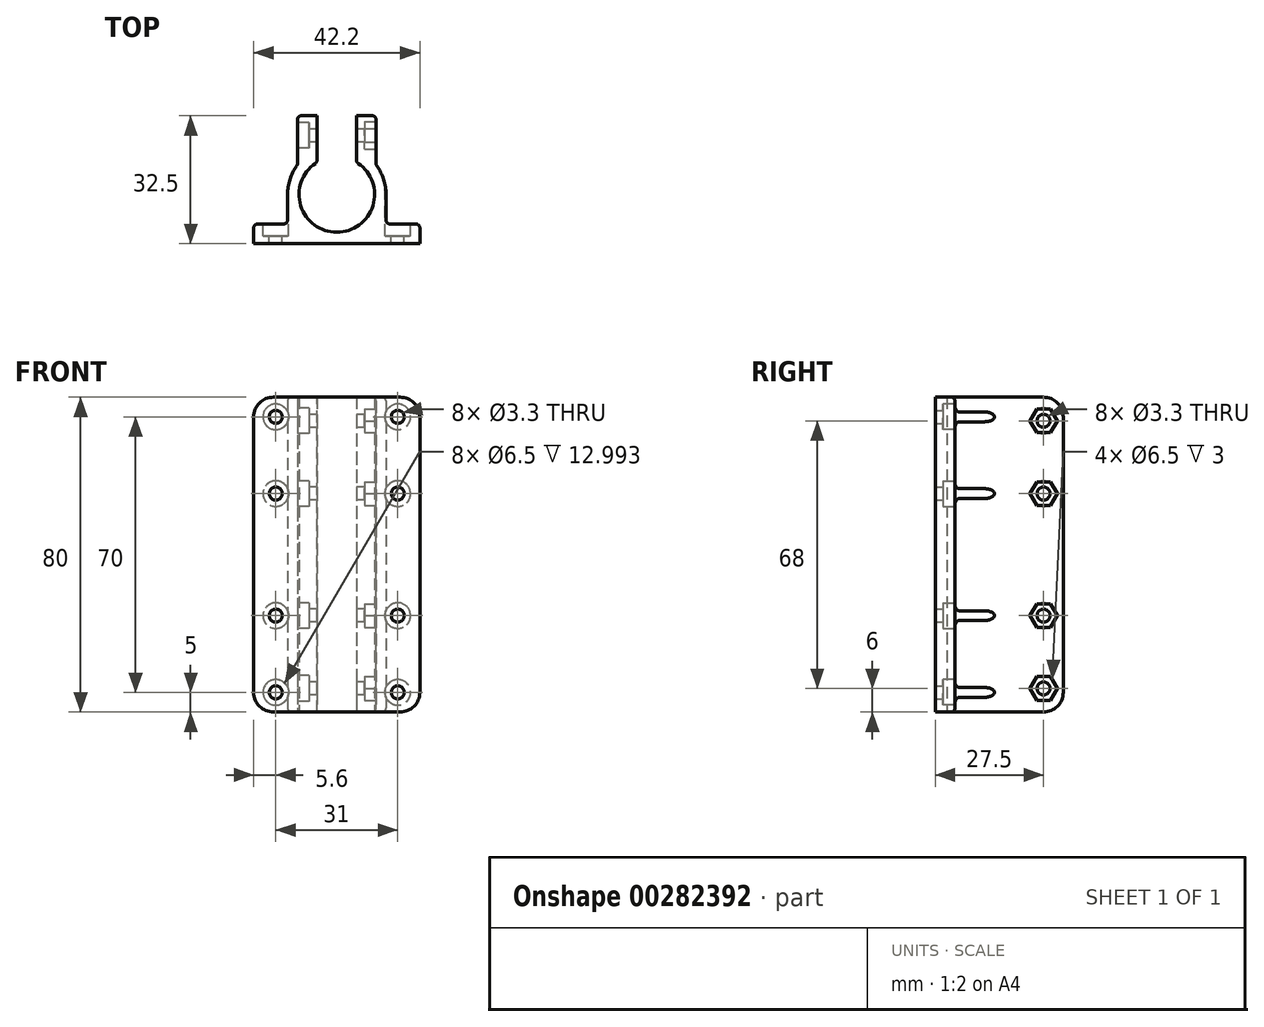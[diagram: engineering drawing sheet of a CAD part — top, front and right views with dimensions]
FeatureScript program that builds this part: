
annotation { "Feature Type Name" : "Feature", "Feature Type Description" : "" }
export const myFeature = defineFeature(function(context is Context, id is Id, definition is map)
    precondition{}
    {
        {
            var Q0;
            Q0=qCreatedBy(makeId("Top.planeOp"),FACE);
            var sketch = newSketch(context, id + "F0", { "sketchPlane" : qUnion([Q0])});
            skArc(sketch, "E0", {"start": v(-5, 8.2) * mm, "mid": v(0, -9.6) * mm, "end": v(5, 8.2) * mm});
            skArc(sketch, "E1", {"start": v(12.5, 0) * mm, "mid": v(11.86, 3.95) * mm, "end": v(10, 7.5) * mm});
            skLineSegment(sketch, "E2", {"start": v(0, 0) * mm, "end": v(0, -12.5) * mm, "construction": true});
            skLineSegment(sketch, "E3", {"start": v(0, -12.5) * mm, "end": v(21.1, -12.5) * mm});
            skLineSegment(sketch, "E4", {"start": v(21.1, -12.5) * mm, "end": v(21.1, -7.5) * mm});
            skLineSegment(sketch, "E5", {"start": v(0, -12.5) * mm, "end": v(-21.1, -12.5) * mm});
            skLineSegment(sketch, "E6", {"start": v(-21.1, -12.5) * mm, "end": v(-21.1, -7.5) * mm});
            skLineSegment(sketch, "E7", {"start": v(-12.5, -7.5) * mm, "end": v(-21.1, -7.5) * mm});
            skLineSegment(sketch, "E8", {"start": v(12.5, -7.5) * mm, "end": v(21.1, -7.5) * mm});
            skLineSegment(sketch, "E9", {"start": v(-12.5, 0) * mm, "end": v(-12.5, -7.5) * mm});
            skLineSegment(sketch, "E10", {"start": v(12.5, 0) * mm, "end": v(12.5, -7.5) * mm});
            skLineSegment(sketch, "E11", {"start": v(0, 0) * mm, "end": v(0, 20) * mm, "construction": true});
            skLineSegment(sketch, "E12.0", {"start": v(-5, 8.2) * mm, "end": v(-5, 20) * mm});
            skLineSegment(sketch, "E13.0", {"start": v(5, 8.2) * mm, "end": v(5, 20) * mm});
            skLineSegment(sketch, "E14.0", {"start": v(10, 7.5) * mm, "end": v(10, 20) * mm});
            skLineSegment(sketch, "E15.0", {"start": v(-10, 7.5) * mm, "end": v(-10, 20) * mm});
            skLineSegment(sketch, "E16", {"start": v(-10, 20) * mm, "end": v(-5, 20) * mm});
            skLineSegment(sketch, "E17", {"start": v(5, 20) * mm, "end": v(10, 20) * mm});
            skArc(sketch, "E18.trimOffspring", {"start": v(-10, 7.5) * mm, "mid": v(-11.86, 3.95) * mm, "end": v(-12.5, 0) * mm});
            skSolve(sketch);
        }
        {
            var Q0;
            Q0=qSketchRegion(id+"F0",true);
            extrude(context, id + "F1", {"entities" : qUnion([Q0]), "depth" : 80 * mm});
        }
        {
            var Q0;
            Q0=makeQuery(id+"F1.opExtrude","SWEPT_FACE",FACE,{"disambiguationData":[OSD([sQuery(id+"F0.wireOp",EDGE,"E8")])]});
            var sketch = newSketch(context, id + "F2", { "sketchPlane" : qUnion([Q0])});
            skLineSegment(sketch, "E19", {"start": v(-15.5, 80) * mm, "end": v(15.5, 80) * mm, "construction": true});
            skLineSegment(sketch, "E20", {"start": v(-21.1, 40) * mm, "end": v(21.1, 40) * mm, "construction": true});
            skLineSegment(sketch, "E21.bottom", {"start": v(15.5, 55.5) * mm, "end": v(-15.5, 55.5) * mm, "construction": true});
            skLineSegment(sketch, "E21.top", {"start": v(15.5, 24.5) * mm, "end": v(-15.5, 24.5) * mm, "construction": true});
            skLineSegment(sketch, "E21.left", {"start": v(15.5, 55.5) * mm, "end": v(15.5, 24.5) * mm, "construction": true});
            skLineSegment(sketch, "E21.right", {"start": v(-15.5, 55.5) * mm, "end": v(-15.5, 24.5) * mm, "construction": true});
            skPoint(sketch, "E21.middle", {"position": v(0, 40) * mm});
            skPoint(sketch, "E22", {"position": v(-15.5, 55.5) * mm});
            skPoint(sketch, "E23", {"position": v(15.5, 55.5) * mm});
            skPoint(sketch, "E24", {"position": v(15.5, 24.5) * mm});
            skPoint(sketch, "E25", {"position": v(-15.5, 24.5) * mm});
            skSolve(sketch);
        }
        {
            var Q0;
            Q0=sQuery(id+"F2.wireOp",VERTEX,"E22");
            var Q1;
            Q1=sQuery(id+"F2.wireOp",VERTEX,"E23");
            var Q2;
            Q2=sQuery(id+"F2.wireOp",VERTEX,"E24");
            var Q3;
            Q3=sQuery(id+"F2.wireOp",VERTEX,"E25");
            var Q4;
            Q4=makeQuery(id+"F1.opExtrude","SWEPT_BODY",BODY,{"disambiguationData":[OSD([sQuery(id+"F0.wireOp",EDGE,"E0"),sQuery(id+"F0.wireOp",EDGE,"E1"),sQuery(id+"F0.wireOp",EDGE,"E3"),sQuery(id+"F0.wireOp",EDGE,"E4"),sQuery(id+"F0.wireOp",EDGE,"E5"),sQuery(id+"F0.wireOp",EDGE,"E6"),sQuery(id+"F0.wireOp",EDGE,"E7"),sQuery(id+"F0.wireOp",EDGE,"E8"),sQuery(id+"F0.wireOp",EDGE,"E9"),sQuery(id+"F0.wireOp",EDGE,"E10")])]});
            hole(context, id + "F3", {"style" : HoleStyle.C_BORE, "endStyle" : HoleEndStyle.THROUGH, "standardTappedOrClearance" : lookupTablePath({ "standard" : "ISO", "fit" : "Normal", "size" : "M3", "type" : "Clearance" }), "standardBlindInLast" : lookupTablePath({ "fit" : "Standard", "standard" : "ISO", "size" : "M3", "type" : "Clearance" }), "holeDiameter" : 3.3 * mm, "cBoreDiameter" : 6.5 * mm, "cBoreDepth" : 3 * mm, "tappedDepth" : 3 * mm, "tapClearance" : 3, "startFromSketch" : true, "locations" : qUnion([Q0, Q1, Q2, Q3]), "scope" : qUnion([Q4])});
        }
        {
            var Q0;
            Q0=makeQuery(id+"F1.opExtrude","SWEPT_FACE",FACE,{"disambiguationData":[OSD([sQuery(id+"F0.wireOp",EDGE,"E8")])]});
            var sketch = newSketch(context, id + "F4", { "sketchPlane" : qUnion([Q0])});
            skPoint(sketch, "E26", {"position": v(-15.5, 5) * mm});
            skPoint(sketch, "E27", {"position": v(15.5, 5) * mm});
            skPoint(sketch, "E28", {"position": v(-15.5, 75) * mm});
            skPoint(sketch, "E29", {"position": v(15.5, 75) * mm});
            skCircle(sketch, "E30", {"center": v(-15.5, 5) * mm, "radius": 3.25 * mm});
            skCircle(sketch, "E31", {"center": v(15.5, 5) * mm, "radius": 3.25 * mm});
            skCircle(sketch, "E32", {"center": v(-15.5, 75) * mm, "radius": 3.25 * mm});
            skCircle(sketch, "E33", {"center": v(15.5, 75) * mm, "radius": 3.25 * mm});
            skLineSegment(sketch, "E34", {"start": v(0, 40) * mm, "end": v(0, 0) * mm, "construction": true});
            skCircle(sketch, "E35", {"center": v(-15.5, 55.5) * mm, "radius": 3.25 * mm});
            skLineSegment(sketch, "E36", {"start": v(-15.5, 5) * mm, "end": v(15.5, 5) * mm, "construction": true});
            skLineSegment(sketch, "E37", {"start": v(-15.5, 75) * mm, "end": v(15.5, 75) * mm, "construction": true});
            skLineSegment(sketch, "E38.bottom", {"start": v(15.5, 55.5) * mm, "end": v(-15.5, 55.5) * mm, "construction": true});
            skLineSegment(sketch, "E38.top", {"start": v(15.5, 24.5) * mm, "end": v(-15.5, 24.5) * mm, "construction": true});
            skLineSegment(sketch, "E38.left", {"start": v(15.5, 55.5) * mm, "end": v(15.5, 24.5) * mm, "construction": true});
            skLineSegment(sketch, "E38.right", {"start": v(-15.5, 55.5) * mm, "end": v(-15.5, 24.5) * mm, "construction": true});
            skPoint(sketch, "E38.middle", {"position": v(0, 40) * mm});
            skCircle(sketch, "E39", {"center": v(15.5, 55.5) * mm, "radius": 3.25 * mm});
            skCircle(sketch, "E40", {"center": v(15.5, 24.5) * mm, "radius": 3.25 * mm});
            skCircle(sketch, "E41", {"center": v(-15.5, 24.5) * mm, "radius": 3.25 * mm});
            skSolve(sketch);
        }
        {
            var Q0;
            Q0=qSketchRegion(id+"F4",true);
            extrude(context, id + "F5", {"entities" : qUnion([Q0]), "operationType" : NewBodyOperationType.REMOVE, "depth" : 25 * mm});
        }
        {
            var Q0;
            Q0=sQuery(id+"F4.wireOp",VERTEX,"E29");
            var Q1;
            Q1=sQuery(id+"F4.wireOp",VERTEX,"E28");
            var Q2;
            Q2=sQuery(id+"F4.wireOp",VERTEX,"E26");
            var Q3;
            Q3=sQuery(id+"F4.wireOp",VERTEX,"E27");
            var Q4;
            Q4=makeQuery(id+"F1.opExtrude","SWEPT_BODY",BODY,{"disambiguationData":[OSD([sQuery(id+"F0.wireOp",EDGE,"E0"),sQuery(id+"F0.wireOp",EDGE,"E1"),sQuery(id+"F0.wireOp",EDGE,"E3"),sQuery(id+"F0.wireOp",EDGE,"E4"),sQuery(id+"F0.wireOp",EDGE,"E5"),sQuery(id+"F0.wireOp",EDGE,"E6"),sQuery(id+"F0.wireOp",EDGE,"E7"),sQuery(id+"F0.wireOp",EDGE,"E8"),sQuery(id+"F0.wireOp",EDGE,"E9"),sQuery(id+"F0.wireOp",EDGE,"E10")])]});
            hole(context, id + "F6", {"style" : HoleStyle.C_BORE, "endStyle" : HoleEndStyle.THROUGH, "standardTappedOrClearance" : lookupTablePath({ "standard" : "ISO", "fit" : "Normal", "size" : "M3", "type" : "Clearance" }), "standardBlindInLast" : lookupTablePath({ "fit" : "Standard", "standard" : "ISO", "size" : "M3", "type" : "Clearance" }), "holeDiameter" : 3.3 * mm, "cBoreDiameter" : 6.5 * mm, "cBoreDepth" : 3 * mm, "tappedDepth" : 3 * mm, "tapClearance" : 3, "startFromSketch" : true, "locations" : qUnion([Q0, Q1, Q2, Q3]), "scope" : qUnion([Q4])});
        }
        {
            var Q0;
            Q0=makeQuery(id+"F1.opExtrude","SWEPT_FACE",FACE,{"disambiguationData":[OSD([sQuery(id+"F0.wireOp",EDGE,"E14.0")])]});
            var sketch = newSketch(context, id + "F7", { "sketchPlane" : qUnion([Q0])});
            skLineSegment(sketch, "E42", {"start": v(15, 80) * mm, "end": v(15, 0) * mm, "construction": true});
            skLineSegment(sketch, "E43", {"start": v(7.5, 40) * mm, "end": v(15, 40) * mm, "construction": true});
            skCircle(sketch, "E44.cCircle", {"center": v(15, 74) * mm, "radius": 3 * mm, "construction": true});
            skLineSegment(sketch, "E44.0", {"start": v(16.73, 71) * mm, "end": v(13.27, 71) * mm});
            skLineSegment(sketch, "E44.1", {"start": v(13.27, 71) * mm, "end": v(11.54, 74) * mm});
            skLineSegment(sketch, "E44.2", {"start": v(11.54, 74) * mm, "end": v(13.27, 77) * mm});
            skLineSegment(sketch, "E44.3", {"start": v(13.27, 77) * mm, "end": v(16.73, 77) * mm});
            skLineSegment(sketch, "E44.4", {"start": v(16.73, 77) * mm, "end": v(18.46, 74) * mm});
            skLineSegment(sketch, "E44.5", {"start": v(18.46, 74) * mm, "end": v(16.73, 71) * mm});
            skPoint(sketch, "E44.0.midPoint", {"position": v(15, 71) * mm});
            skCircle(sketch, "E45.cCircle", {"center": v(15, 55.5) * mm, "radius": 3 * mm, "construction": true});
            skLineSegment(sketch, "E45.0", {"start": v(16.73, 52.5) * mm, "end": v(13.27, 52.5) * mm});
            skLineSegment(sketch, "E45.1", {"start": v(13.27, 52.5) * mm, "end": v(11.54, 55.5) * mm});
            skLineSegment(sketch, "E45.2", {"start": v(11.54, 55.5) * mm, "end": v(13.27, 58.5) * mm});
            skLineSegment(sketch, "E45.3", {"start": v(13.27, 58.5) * mm, "end": v(16.73, 58.5) * mm});
            skLineSegment(sketch, "E45.4", {"start": v(16.73, 58.5) * mm, "end": v(18.46, 55.5) * mm});
            skLineSegment(sketch, "E45.5", {"start": v(18.46, 55.5) * mm, "end": v(16.73, 52.5) * mm});
            skPoint(sketch, "E45.0.midPoint", {"position": v(15, 52.5) * mm});
            skCircle(sketch, "E46.cCircle", {"center": v(15, 24.5) * mm, "radius": 3 * mm, "construction": true});
            skLineSegment(sketch, "E46.0", {"start": v(16.73, 21.5) * mm, "end": v(13.27, 21.5) * mm});
            skLineSegment(sketch, "E46.1", {"start": v(13.27, 21.5) * mm, "end": v(11.54, 24.5) * mm});
            skLineSegment(sketch, "E46.2", {"start": v(11.54, 24.5) * mm, "end": v(13.27, 27.5) * mm});
            skLineSegment(sketch, "E46.3", {"start": v(13.27, 27.5) * mm, "end": v(16.73, 27.5) * mm});
            skLineSegment(sketch, "E46.4", {"start": v(16.73, 27.5) * mm, "end": v(18.46, 24.5) * mm});
            skLineSegment(sketch, "E46.5", {"start": v(18.46, 24.5) * mm, "end": v(16.73, 21.5) * mm});
            skPoint(sketch, "E46.0.midPoint", {"position": v(15, 21.5) * mm});
            skCircle(sketch, "E47.cCircle", {"center": v(15, 6) * mm, "radius": 3 * mm, "construction": true});
            skLineSegment(sketch, "E47.0", {"start": v(16.73, 3) * mm, "end": v(13.27, 3) * mm});
            skLineSegment(sketch, "E47.1", {"start": v(13.27, 3) * mm, "end": v(11.54, 6) * mm});
            skLineSegment(sketch, "E47.2", {"start": v(11.54, 6) * mm, "end": v(13.27, 9) * mm});
            skLineSegment(sketch, "E47.3", {"start": v(13.27, 9) * mm, "end": v(16.73, 9) * mm});
            skLineSegment(sketch, "E47.4", {"start": v(16.73, 9) * mm, "end": v(18.46, 6) * mm});
            skLineSegment(sketch, "E47.5", {"start": v(18.46, 6) * mm, "end": v(16.73, 3) * mm});
            skPoint(sketch, "E47.0.midPoint", {"position": v(15, 3) * mm});
            skSolve(sketch);
        }
        {
            var Q0;
            Q0 = qSketchRegion(id + "F7", true);
            extrude(context, id + "F8", {"entities" : qUnion([Q0]), "operationType" : NewBodyOperationType.REMOVE, "oppositeDirection" : true, "depth" : 3 * mm});
        }
        {
            var Q0;
            Q0=makeQuery(id+"F1.opExtrude","SWEPT_FACE",FACE,{"disambiguationData":[OSD([sQuery(id+"F0.wireOp",EDGE,"E15.0")])]});
            var sketch = newSketch(context, id + "F9", { "sketchPlane" : qUnion([Q0])});
            skLineSegment(sketch, "E48", {"start": v(-15, 80) * mm, "end": v(-15, 0) * mm, "construction": true});
            skLineSegment(sketch, "E49", {"start": v(-15, 40) * mm, "end": v(-7.5, 40) * mm, "construction": true});
            skPoint(sketch, "E50", {"position": v(-15, 74) * mm});
            skPoint(sketch, "E51", {"position": v(-15, 55.5) * mm});
            skPoint(sketch, "E52", {"position": v(-15, 24.5) * mm});
            skPoint(sketch, "E53", {"position": v(-15, 6) * mm});
            skSolve(sketch);
        }
        {
            var Q0;
            Q0=sQuery(id+"F9.wireOp",VERTEX,"E50");
            var Q1;
            Q1=sQuery(id+"F9.wireOp",VERTEX,"E51");
            var Q2;
            Q2=sQuery(id+"F9.wireOp",VERTEX,"E52");
            var Q3;
            Q3=sQuery(id+"F9.wireOp",VERTEX,"E53");
            var Q4;
            Q4=makeQuery(id+"F1.opExtrude","SWEPT_BODY",BODY,{"disambiguationData":[OSD([sQuery(id+"F0.wireOp",EDGE,"E0"),sQuery(id+"F0.wireOp",EDGE,"E1"),sQuery(id+"F0.wireOp",EDGE,"E3"),sQuery(id+"F0.wireOp",EDGE,"E4"),sQuery(id+"F0.wireOp",EDGE,"E5"),sQuery(id+"F0.wireOp",EDGE,"E6"),sQuery(id+"F0.wireOp",EDGE,"E7"),sQuery(id+"F0.wireOp",EDGE,"E8"),sQuery(id+"F0.wireOp",EDGE,"E9"),sQuery(id+"F0.wireOp",EDGE,"E10"),sQuery(id+"F0.wireOp",EDGE,"E12.0"),sQuery(id+"F0.wireOp",EDGE,"E13.0"),sQuery(id+"F0.wireOp",EDGE,"E14.0"),sQuery(id+"F0.wireOp",EDGE,"E15.0"),sQuery(id+"F0.wireOp",EDGE,"E16"),sQuery(id+"F0.wireOp",EDGE,"E17"),sQuery(id+"F0.wireOp",EDGE,"E18.trimOffspring")])]});
            hole(context, id + "F10", {"style" : HoleStyle.C_BORE, "endStyle" : HoleEndStyle.THROUGH, "standardTappedOrClearance" : lookupTablePath({ "standard" : "ISO", "fit" : "Normal", "size" : "M3", "type" : "Clearance" }), "standardBlindInLast" : lookupTablePath({ "fit" : "Standard", "standard" : "ISO", "size" : "M3", "type" : "Clearance" }), "holeDiameter" : 3.3 * mm, "cBoreDiameter" : 6.5 * mm, "cBoreDepth" : 3 * mm, "tappedDepth" : 3 * mm, "tapClearance" : 3, "startFromSketch" : true, "locations" : qUnion([Q0, Q1, Q2, Q3]), "scope" : qUnion([Q4])});
        }
        {
            var Q0;
            Q0=makeQuery(id+"F1.opExtrude","CAP_EDGE",EDGE,{"disambiguationData":[OSD([sQuery(id+"F0.wireOp",EDGE,"E17")])],"isStart":true});
            var Q1;
            Q1=makeQuery(id+"F1.opExtrude","CAP_EDGE",EDGE,{"disambiguationData":[OSD([sQuery(id+"F0.wireOp",EDGE,"E16")])],"isStart":true});
            var Q2;
            Q2=makeQuery(id+"F1.opExtrude","CAP_EDGE",EDGE,{"disambiguationData":[OSD([sQuery(id+"F0.wireOp",EDGE,"E6")])],"isStart":true});
            var Q3;
            Q3=makeQuery(id+"F1.opExtrude","CAP_EDGE",EDGE,{"disambiguationData":[OSD([sQuery(id+"F0.wireOp",EDGE,"E4")])],"isStart":true});
            var Q4;
            Q4=makeQuery(id+"F1.opExtrude","CAP_EDGE",EDGE,{"disambiguationData":[OSD([sQuery(id+"F0.wireOp",EDGE,"E17")])],"isStart":false});
            var Q5;
            Q5=makeQuery(id+"F1.opExtrude","CAP_EDGE",EDGE,{"disambiguationData":[OSD([sQuery(id+"F0.wireOp",EDGE,"E16")])],"isStart":false});
            var Q6;
            Q6=makeQuery(id+"F1.opExtrude","CAP_EDGE",EDGE,{"disambiguationData":[OSD([sQuery(id+"F0.wireOp",EDGE,"E4")])],"isStart":false});
            var Q7;
            Q7=makeQuery(id+"F1.opExtrude","CAP_EDGE",EDGE,{"disambiguationData":[OSD([sQuery(id+"F0.wireOp",EDGE,"E6")])],"isStart":false});
            fillet(context, id + "F11", {"entities" : qUnion([Q0, Q1, Q2, Q3, Q4, Q5, Q6, Q7]), "radius" : 5 * mm, "tangentPropagation" : true, "allowEdgeOverflow" : false});
        }
        {
            var Q0;
            {var subQ0=sQuery(id+"F0.wireOp",EDGE,"E10");var subQ1=sQuery(id+"F0.wireOp",EDGE,"E8");var subQ2=makeQuery(id+"F1.opExtrude","CAP_FACE",FACE,{"disambiguationData":[OSD([sQuery(id+"F0.wireOp",EDGE,"E0"),sQuery(id+"F0.wireOp",EDGE,"E1"),sQuery(id+"F0.wireOp",EDGE,"E3"),sQuery(id+"F0.wireOp",EDGE,"E4"),sQuery(id+"F0.wireOp",EDGE,"E5"),sQuery(id+"F0.wireOp",EDGE,"E6"),sQuery(id+"F0.wireOp",EDGE,"E7"),subQ1,sQuery(id+"F0.wireOp",EDGE,"E9"),subQ0,sQuery(id+"F0.wireOp",EDGE,"E12.0"),sQuery(id+"F0.wireOp",EDGE,"E13.0"),sQuery(id+"F0.wireOp",EDGE,"E14.0"),sQuery(id+"F0.wireOp",EDGE,"E15.0"),sQuery(id+"F0.wireOp",EDGE,"E16"),sQuery(id+"F0.wireOp",EDGE,"E17"),sQuery(id+"F0.wireOp",EDGE,"E18.trimOffspring")])],"isStart":false});var subQ3=makeQuery(id+"F1.opExtrude","SWEPT_FACE",FACE,{"disambiguationData":[OSD([subQ0])]});var subQ4=makeQuery(id+"F1.opExtrude","SWEPT_FACE",FACE,{"disambiguationData":[OSD([subQ1])]});Q0=makeQuery(id+"F5.boolean.opBoolean","SPLIT",EDGE,{"disambiguationData":[TD([subQ2])],"derivedFrom":makeQuery(id+"F3.hole-0.boolean.opBoolean","SPLIT",EDGE,{"disambiguationData":[topologyDisambiguationEdgeConnected([subQ4,subQ3]),TD([subQ2])],"derivedFrom":makeQuery(id+"F1.opExtrude","SWEPT_EDGE",EDGE,{"disambiguationData":[OSD([subQ1,subQ0])]})})});}
            var Q1;
            {var subQ0=makeQuery(id+"F3.hole-0.opRevolve","SWEPT_FACE",FACE,{"disambiguationData":[OSD([sQuery(id+"F3.hole-0.sketch.wireOp",EDGE,"cbore_start_line_2")])]});var subQ1=sQuery(id+"F0.wireOp",EDGE,"E10");var subQ2=makeQuery(id+"F1.opExtrude","SWEPT_FACE",FACE,{"disambiguationData":[OSD([subQ1])]});var subQ3=sQuery(id+"F0.wireOp",EDGE,"E8");var subQ4=makeQuery(id+"F1.opExtrude","SWEPT_FACE",FACE,{"disambiguationData":[OSD([subQ3])]});Q1=makeQuery(id+"F5.boolean.opBoolean","SPLIT",EDGE,{"disambiguationData":[TD([makeQuery(id+"F3.hole-0.boolean.opBoolean","COPY",FACE,{"derivedFrom":subQ0})])],"derivedFrom":makeQuery(id+"F3.hole-0.boolean.opBoolean","SPLIT",EDGE,{"disambiguationData":[topologyDisambiguationEdgeConnected([subQ4,subQ2]),TD([makeQuery(id+"F1.opExtrude","CAP_FACE",FACE,{"disambiguationData":[OSD([sQuery(id+"F0.wireOp",EDGE,"E0"),sQuery(id+"F0.wireOp",EDGE,"E1"),sQuery(id+"F0.wireOp",EDGE,"E3"),sQuery(id+"F0.wireOp",EDGE,"E4"),sQuery(id+"F0.wireOp",EDGE,"E5"),sQuery(id+"F0.wireOp",EDGE,"E6"),sQuery(id+"F0.wireOp",EDGE,"E7"),subQ3,sQuery(id+"F0.wireOp",EDGE,"E9"),subQ1,sQuery(id+"F0.wireOp",EDGE,"E12.0"),sQuery(id+"F0.wireOp",EDGE,"E13.0"),sQuery(id+"F0.wireOp",EDGE,"E14.0"),sQuery(id+"F0.wireOp",EDGE,"E15.0"),sQuery(id+"F0.wireOp",EDGE,"E16"),sQuery(id+"F0.wireOp",EDGE,"E17"),sQuery(id+"F0.wireOp",EDGE,"E18.trimOffspring")])],"isStart":false})])],"derivedFrom":makeQuery(id+"F1.opExtrude","SWEPT_EDGE",EDGE,{"disambiguationData":[OSD([subQ3,subQ1])]})})});}
            var Q2;
            {var subQ1=sQuery(id+"F0.wireOp",EDGE,"E10");var subQ2=sQuery(id+"F0.wireOp",EDGE,"E8");var subQ3=makeQuery(id+"F1.opExtrude","CAP_FACE",FACE,{"disambiguationData":[OSD([sQuery(id+"F0.wireOp",EDGE,"E0"),sQuery(id+"F0.wireOp",EDGE,"E1"),sQuery(id+"F0.wireOp",EDGE,"E3"),sQuery(id+"F0.wireOp",EDGE,"E4"),sQuery(id+"F0.wireOp",EDGE,"E5"),sQuery(id+"F0.wireOp",EDGE,"E6"),sQuery(id+"F0.wireOp",EDGE,"E7"),subQ2,sQuery(id+"F0.wireOp",EDGE,"E9"),subQ1,sQuery(id+"F0.wireOp",EDGE,"E12.0"),sQuery(id+"F0.wireOp",EDGE,"E13.0"),sQuery(id+"F0.wireOp",EDGE,"E14.0"),sQuery(id+"F0.wireOp",EDGE,"E15.0"),sQuery(id+"F0.wireOp",EDGE,"E16"),sQuery(id+"F0.wireOp",EDGE,"E17"),sQuery(id+"F0.wireOp",EDGE,"E18.trimOffspring")])],"isStart":true});var subQ4=makeQuery(id+"F1.opExtrude","SWEPT_FACE",FACE,{"disambiguationData":[OSD([subQ1])]});var subQ5=makeQuery(id+"F1.opExtrude","SWEPT_FACE",FACE,{"disambiguationData":[OSD([subQ2])]});Q2=makeQuery(id+"F5.boolean.opBoolean","SPLIT",EDGE,{"disambiguationData":[TD([subQ3])],"derivedFrom":makeQuery(id+"F3.hole-3.boolean.opBoolean","SPLIT",EDGE,{"disambiguationData":[topologyDisambiguationEdgeConnected([subQ5,subQ4]),TD([subQ3])],"derivedFrom":makeQuery(id+"F3.hole-0.boolean.opBoolean","SPLIT",EDGE,{"disambiguationData":[topologyDisambiguationEdgeConnected([subQ5,subQ4]),TD([subQ3])],"derivedFrom":makeQuery(id+"F1.opExtrude","SWEPT_EDGE",EDGE,{"disambiguationData":[OSD([subQ2,subQ1])]})})})});}
            var Q3;
            {var subQ1=sQuery(id+"F0.wireOp",EDGE,"E9");var subQ2=makeQuery(id+"F1.opExtrude","SWEPT_FACE",FACE,{"disambiguationData":[OSD([subQ1])]});var subQ3=sQuery(id+"F0.wireOp",EDGE,"E7");var subQ4=makeQuery(id+"F1.opExtrude","SWEPT_FACE",FACE,{"disambiguationData":[OSD([subQ3])]});var subQ5=makeQuery(id+"F1.opExtrude","CAP_FACE",FACE,{"disambiguationData":[OSD([sQuery(id+"F0.wireOp",EDGE,"E0"),sQuery(id+"F0.wireOp",EDGE,"E1"),sQuery(id+"F0.wireOp",EDGE,"E3"),sQuery(id+"F0.wireOp",EDGE,"E4"),sQuery(id+"F0.wireOp",EDGE,"E5"),sQuery(id+"F0.wireOp",EDGE,"E6"),subQ3,sQuery(id+"F0.wireOp",EDGE,"E8"),subQ1,sQuery(id+"F0.wireOp",EDGE,"E10"),sQuery(id+"F0.wireOp",EDGE,"E12.0"),sQuery(id+"F0.wireOp",EDGE,"E13.0"),sQuery(id+"F0.wireOp",EDGE,"E14.0"),sQuery(id+"F0.wireOp",EDGE,"E15.0"),sQuery(id+"F0.wireOp",EDGE,"E16"),sQuery(id+"F0.wireOp",EDGE,"E17"),sQuery(id+"F0.wireOp",EDGE,"E18.trimOffspring")])],"isStart":true});Q3=makeQuery(id+"F5.boolean.opBoolean","SPLIT",EDGE,{"disambiguationData":[TD([subQ5])],"derivedFrom":makeQuery(id+"F3.hole-2.boolean.opBoolean","SPLIT",EDGE,{"disambiguationData":[topologyDisambiguationEdgeConnected([subQ4,subQ2]),TD([subQ5])],"derivedFrom":makeQuery(id+"F3.hole-1.boolean.opBoolean","SPLIT",EDGE,{"disambiguationData":[topologyDisambiguationEdgeConnected([subQ4,subQ2]),TD([subQ5])],"derivedFrom":makeQuery(id+"F1.opExtrude","SWEPT_EDGE",EDGE,{"disambiguationData":[OSD([subQ3,subQ1])]})})})});}
            var Q4;
            {var subQ0=sQuery(id+"F0.wireOp",EDGE,"E9");var subQ1=makeQuery(id+"F1.opExtrude","SWEPT_FACE",FACE,{"disambiguationData":[OSD([subQ0])]});var subQ2=makeQuery(id+"F3.hole-1.opRevolve","SWEPT_FACE",FACE,{"disambiguationData":[OSD([sQuery(id+"F3.hole-1.sketch.wireOp",EDGE,"cbore_start_line_2")])]});var subQ3=sQuery(id+"F0.wireOp",EDGE,"E7");var subQ4=makeQuery(id+"F1.opExtrude","SWEPT_FACE",FACE,{"disambiguationData":[OSD([subQ3])]});Q4=makeQuery(id+"F5.boolean.opBoolean","SPLIT",EDGE,{"disambiguationData":[TD([makeQuery(id+"F3.hole-1.boolean.opBoolean","COPY",FACE,{"derivedFrom":subQ2})])],"derivedFrom":makeQuery(id+"F3.hole-1.boolean.opBoolean","SPLIT",EDGE,{"disambiguationData":[topologyDisambiguationEdgeConnected([subQ4,subQ1]),TD([makeQuery(id+"F1.opExtrude","CAP_FACE",FACE,{"disambiguationData":[OSD([sQuery(id+"F0.wireOp",EDGE,"E0"),sQuery(id+"F0.wireOp",EDGE,"E1"),sQuery(id+"F0.wireOp",EDGE,"E3"),sQuery(id+"F0.wireOp",EDGE,"E4"),sQuery(id+"F0.wireOp",EDGE,"E5"),sQuery(id+"F0.wireOp",EDGE,"E6"),subQ3,sQuery(id+"F0.wireOp",EDGE,"E8"),subQ0,sQuery(id+"F0.wireOp",EDGE,"E10"),sQuery(id+"F0.wireOp",EDGE,"E12.0"),sQuery(id+"F0.wireOp",EDGE,"E13.0"),sQuery(id+"F0.wireOp",EDGE,"E14.0"),sQuery(id+"F0.wireOp",EDGE,"E15.0"),sQuery(id+"F0.wireOp",EDGE,"E16"),sQuery(id+"F0.wireOp",EDGE,"E17"),sQuery(id+"F0.wireOp",EDGE,"E18.trimOffspring")])],"isStart":false})])],"derivedFrom":makeQuery(id+"F1.opExtrude","SWEPT_EDGE",EDGE,{"disambiguationData":[OSD([subQ3,subQ0])]})})});}
            var Q5;
            {var subQ0=sQuery(id+"F0.wireOp",EDGE,"E9");var subQ1=makeQuery(id+"F1.opExtrude","SWEPT_FACE",FACE,{"disambiguationData":[OSD([subQ0])]});var subQ2=sQuery(id+"F0.wireOp",EDGE,"E7");var subQ3=makeQuery(id+"F1.opExtrude","SWEPT_FACE",FACE,{"disambiguationData":[OSD([subQ2])]});var subQ4=makeQuery(id+"F1.opExtrude","CAP_FACE",FACE,{"disambiguationData":[OSD([sQuery(id+"F0.wireOp",EDGE,"E0"),sQuery(id+"F0.wireOp",EDGE,"E1"),sQuery(id+"F0.wireOp",EDGE,"E3"),sQuery(id+"F0.wireOp",EDGE,"E4"),sQuery(id+"F0.wireOp",EDGE,"E5"),sQuery(id+"F0.wireOp",EDGE,"E6"),subQ2,sQuery(id+"F0.wireOp",EDGE,"E8"),subQ0,sQuery(id+"F0.wireOp",EDGE,"E10"),sQuery(id+"F0.wireOp",EDGE,"E12.0"),sQuery(id+"F0.wireOp",EDGE,"E13.0"),sQuery(id+"F0.wireOp",EDGE,"E14.0"),sQuery(id+"F0.wireOp",EDGE,"E15.0"),sQuery(id+"F0.wireOp",EDGE,"E16"),sQuery(id+"F0.wireOp",EDGE,"E17"),sQuery(id+"F0.wireOp",EDGE,"E18.trimOffspring")])],"isStart":false});Q5=makeQuery(id+"F5.boolean.opBoolean","SPLIT",EDGE,{"disambiguationData":[TD([subQ4])],"derivedFrom":makeQuery(id+"F3.hole-1.boolean.opBoolean","SPLIT",EDGE,{"disambiguationData":[topologyDisambiguationEdgeConnected([subQ3,subQ1]),TD([subQ4])],"derivedFrom":makeQuery(id+"F1.opExtrude","SWEPT_EDGE",EDGE,{"disambiguationData":[OSD([subQ2,subQ0])]})})});}
            var Q6;
            Q6=makeQuery(id+"F1.opExtrude","SWEPT_EDGE",EDGE,{"disambiguationData":[OSD([sQuery(id+"F0.wireOp",EDGE,"E15.0"),sQuery(id+"F0.wireOp",EDGE,"E18.trimOffspring")])]});
            var Q7;
            Q7=makeQuery(id+"F1.opExtrude","SWEPT_EDGE",EDGE,{"disambiguationData":[OSD([sQuery(id+"F0.wireOp",EDGE,"E0"),sQuery(id+"F0.wireOp",EDGE,"E12.0")])]});
            var Q8;
            Q8=makeQuery(id+"F1.opExtrude","SWEPT_EDGE",EDGE,{"disambiguationData":[OSD([sQuery(id+"F0.wireOp",EDGE,"E0"),sQuery(id+"F0.wireOp",EDGE,"E13.0")])]});
            var Q9;
            Q9=makeQuery(id+"F1.opExtrude","SWEPT_EDGE",EDGE,{"disambiguationData":[OSD([sQuery(id+"F0.wireOp",EDGE,"E1"),sQuery(id+"F0.wireOp",EDGE,"E14.0")])]});
            var Q10;
            {var subQ0=makeQuery(id+"F3.hole-0.opRevolve","SWEPT_FACE",FACE,{"disambiguationData":[OSD([sQuery(id+"F3.hole-0.sketch.wireOp",EDGE,"cbore_start_line_2")])]});var subQ1=sQuery(id+"F0.wireOp",EDGE,"E10");var subQ2=makeQuery(id+"F1.opExtrude","SWEPT_FACE",FACE,{"disambiguationData":[OSD([subQ1])]});var subQ4=sQuery(id+"F0.wireOp",EDGE,"E8");var subQ5=makeQuery(id+"F1.opExtrude","SWEPT_FACE",FACE,{"disambiguationData":[OSD([subQ4])]});Q10=makeQuery(id+"F3.hole-3.boolean.opBoolean","SPLIT",EDGE,{"disambiguationData":[topologyDisambiguationEdgeConnected([subQ5,subQ2]),TD([makeQuery(id+"F3.hole-0.boolean.opBoolean","COPY",FACE,{"derivedFrom":subQ0})])],"derivedFrom":makeQuery(id+"F3.hole-0.boolean.opBoolean","SPLIT",EDGE,{"disambiguationData":[topologyDisambiguationEdgeConnected([subQ5,subQ2]),TD([makeQuery(id+"F1.opExtrude","CAP_FACE",FACE,{"disambiguationData":[OSD([sQuery(id+"F0.wireOp",EDGE,"E0"),sQuery(id+"F0.wireOp",EDGE,"E1"),sQuery(id+"F0.wireOp",EDGE,"E3"),sQuery(id+"F0.wireOp",EDGE,"E4"),sQuery(id+"F0.wireOp",EDGE,"E5"),sQuery(id+"F0.wireOp",EDGE,"E6"),sQuery(id+"F0.wireOp",EDGE,"E7"),subQ4,sQuery(id+"F0.wireOp",EDGE,"E9"),subQ1,sQuery(id+"F0.wireOp",EDGE,"E12.0"),sQuery(id+"F0.wireOp",EDGE,"E13.0"),sQuery(id+"F0.wireOp",EDGE,"E14.0"),sQuery(id+"F0.wireOp",EDGE,"E15.0"),sQuery(id+"F0.wireOp",EDGE,"E16"),sQuery(id+"F0.wireOp",EDGE,"E17"),sQuery(id+"F0.wireOp",EDGE,"E18.trimOffspring")])],"isStart":true})])],"derivedFrom":makeQuery(id+"F1.opExtrude","SWEPT_EDGE",EDGE,{"disambiguationData":[OSD([subQ4,subQ1])]})})});}
            var Q11;
            {var subQ0=makeQuery(id+"F3.hole-3.opRevolve","SWEPT_FACE",FACE,{"disambiguationData":[OSD([sQuery(id+"F3.hole-3.sketch.wireOp",EDGE,"cbore_start_line_2")])]});var subQ1=sQuery(id+"F0.wireOp",EDGE,"E8");var subQ2=makeQuery(id+"F1.opExtrude","SWEPT_FACE",FACE,{"disambiguationData":[OSD([subQ1])]});var subQ4=sQuery(id+"F0.wireOp",EDGE,"E10");var subQ5=makeQuery(id+"F1.opExtrude","SWEPT_FACE",FACE,{"disambiguationData":[OSD([subQ4])]});var subQ6=makeQuery(id+"F1.opExtrude","CAP_FACE",FACE,{"disambiguationData":[OSD([sQuery(id+"F0.wireOp",EDGE,"E0"),sQuery(id+"F0.wireOp",EDGE,"E1"),sQuery(id+"F0.wireOp",EDGE,"E3"),sQuery(id+"F0.wireOp",EDGE,"E4"),sQuery(id+"F0.wireOp",EDGE,"E5"),sQuery(id+"F0.wireOp",EDGE,"E6"),sQuery(id+"F0.wireOp",EDGE,"E7"),subQ1,sQuery(id+"F0.wireOp",EDGE,"E9"),subQ4,sQuery(id+"F0.wireOp",EDGE,"E12.0"),sQuery(id+"F0.wireOp",EDGE,"E13.0"),sQuery(id+"F0.wireOp",EDGE,"E14.0"),sQuery(id+"F0.wireOp",EDGE,"E15.0"),sQuery(id+"F0.wireOp",EDGE,"E16"),sQuery(id+"F0.wireOp",EDGE,"E17"),sQuery(id+"F0.wireOp",EDGE,"E18.trimOffspring")])],"isStart":true});Q11=makeQuery(id+"F5.boolean.opBoolean","SPLIT",EDGE,{"disambiguationData":[TD([makeQuery(id+"F3.hole-3.boolean.opBoolean","COPY",FACE,{"derivedFrom":subQ0})])],"derivedFrom":makeQuery(id+"F3.hole-3.boolean.opBoolean","SPLIT",EDGE,{"disambiguationData":[topologyDisambiguationEdgeConnected([subQ2,subQ5]),TD([subQ6])],"derivedFrom":makeQuery(id+"F3.hole-0.boolean.opBoolean","SPLIT",EDGE,{"disambiguationData":[topologyDisambiguationEdgeConnected([subQ2,subQ5]),TD([subQ6])],"derivedFrom":makeQuery(id+"F1.opExtrude","SWEPT_EDGE",EDGE,{"disambiguationData":[OSD([subQ1,subQ4])]})})})});}
            var Q12;
            {var subQ1=sQuery(id+"F0.wireOp",EDGE,"E9");var subQ2=makeQuery(id+"F1.opExtrude","SWEPT_FACE",FACE,{"disambiguationData":[OSD([subQ1])]});var subQ3=makeQuery(id+"F3.hole-2.opRevolve","SWEPT_FACE",FACE,{"disambiguationData":[OSD([sQuery(id+"F3.hole-2.sketch.wireOp",EDGE,"cbore_start_line_2")])]});var subQ4=sQuery(id+"F0.wireOp",EDGE,"E7");var subQ5=makeQuery(id+"F1.opExtrude","SWEPT_FACE",FACE,{"disambiguationData":[OSD([subQ4])]});var subQ6=makeQuery(id+"F1.opExtrude","CAP_FACE",FACE,{"disambiguationData":[OSD([sQuery(id+"F0.wireOp",EDGE,"E0"),sQuery(id+"F0.wireOp",EDGE,"E1"),sQuery(id+"F0.wireOp",EDGE,"E3"),sQuery(id+"F0.wireOp",EDGE,"E4"),sQuery(id+"F0.wireOp",EDGE,"E5"),sQuery(id+"F0.wireOp",EDGE,"E6"),subQ4,sQuery(id+"F0.wireOp",EDGE,"E8"),subQ1,sQuery(id+"F0.wireOp",EDGE,"E10"),sQuery(id+"F0.wireOp",EDGE,"E12.0"),sQuery(id+"F0.wireOp",EDGE,"E13.0"),sQuery(id+"F0.wireOp",EDGE,"E14.0"),sQuery(id+"F0.wireOp",EDGE,"E15.0"),sQuery(id+"F0.wireOp",EDGE,"E16"),sQuery(id+"F0.wireOp",EDGE,"E17"),sQuery(id+"F0.wireOp",EDGE,"E18.trimOffspring")])],"isStart":true});Q12=makeQuery(id+"F5.boolean.opBoolean","SPLIT",EDGE,{"disambiguationData":[TD([makeQuery(id+"F3.hole-2.boolean.opBoolean","COPY",FACE,{"derivedFrom":subQ3})])],"derivedFrom":makeQuery(id+"F3.hole-2.boolean.opBoolean","SPLIT",EDGE,{"disambiguationData":[topologyDisambiguationEdgeConnected([subQ5,subQ2]),TD([subQ6])],"derivedFrom":makeQuery(id+"F3.hole-1.boolean.opBoolean","SPLIT",EDGE,{"disambiguationData":[topologyDisambiguationEdgeConnected([subQ5,subQ2]),TD([subQ6])],"derivedFrom":makeQuery(id+"F1.opExtrude","SWEPT_EDGE",EDGE,{"disambiguationData":[OSD([subQ4,subQ1])]})})})});}
            var Q13;
            {var subQ1=sQuery(id+"F0.wireOp",EDGE,"E9");var subQ2=makeQuery(id+"F1.opExtrude","SWEPT_FACE",FACE,{"disambiguationData":[OSD([subQ1])]});var subQ3=makeQuery(id+"F3.hole-1.opRevolve","SWEPT_FACE",FACE,{"disambiguationData":[OSD([sQuery(id+"F3.hole-1.sketch.wireOp",EDGE,"cbore_start_line_2")])]});var subQ4=sQuery(id+"F0.wireOp",EDGE,"E7");var subQ5=makeQuery(id+"F1.opExtrude","SWEPT_FACE",FACE,{"disambiguationData":[OSD([subQ4])]});Q13=makeQuery(id+"F3.hole-2.boolean.opBoolean","SPLIT",EDGE,{"disambiguationData":[topologyDisambiguationEdgeConnected([subQ5,subQ2]),TD([makeQuery(id+"F3.hole-1.boolean.opBoolean","COPY",FACE,{"derivedFrom":subQ3})])],"derivedFrom":makeQuery(id+"F3.hole-1.boolean.opBoolean","SPLIT",EDGE,{"disambiguationData":[topologyDisambiguationEdgeConnected([subQ5,subQ2]),TD([makeQuery(id+"F1.opExtrude","CAP_FACE",FACE,{"disambiguationData":[OSD([sQuery(id+"F0.wireOp",EDGE,"E0"),sQuery(id+"F0.wireOp",EDGE,"E1"),sQuery(id+"F0.wireOp",EDGE,"E3"),sQuery(id+"F0.wireOp",EDGE,"E4"),sQuery(id+"F0.wireOp",EDGE,"E5"),sQuery(id+"F0.wireOp",EDGE,"E6"),subQ4,sQuery(id+"F0.wireOp",EDGE,"E8"),subQ1,sQuery(id+"F0.wireOp",EDGE,"E10"),sQuery(id+"F0.wireOp",EDGE,"E12.0"),sQuery(id+"F0.wireOp",EDGE,"E13.0"),sQuery(id+"F0.wireOp",EDGE,"E14.0"),sQuery(id+"F0.wireOp",EDGE,"E15.0"),sQuery(id+"F0.wireOp",EDGE,"E16"),sQuery(id+"F0.wireOp",EDGE,"E17"),sQuery(id+"F0.wireOp",EDGE,"E18.trimOffspring")])],"isStart":true})])],"derivedFrom":makeQuery(id+"F1.opExtrude","SWEPT_EDGE",EDGE,{"disambiguationData":[OSD([subQ4,subQ1])]})})});}
            fillet(context, id + "F12", {"entities" : qUnion([Q0, Q1, Q2, Q3, Q4, Q5, Q6, Q7, Q8, Q9, Q10, Q11, Q12, Q13]), "radius" : 1 * mm, "allowEdgeOverflow" : false});
        }
        {
            var Q0;
            Q0=makeQuery(id+"F11.opFillet","BLEND_EDGE",EDGE,{"blendedFrom":[makeQuery(id+"F1.opExtrude","CAP_EDGE",EDGE,{"disambiguationData":[OSD([sQuery(id+"F0.wireOp",EDGE,"E4")])],"isStart":true}),makeQuery(id+"F5.boolean.opBoolean","MERGE",FACE,{"derivedFrom":[makeQuery(id+"F1.opExtrude","SWEPT_FACE",FACE,{"disambiguationData":[OSD([sQuery(id+"F0.wireOp",EDGE,"E8")])]}),makeQuery(id+"F5.opExtrude","CAP_FACE",FACE,{"disambiguationData":[OSD([sQuery(id+"F4.wireOp",EDGE,"E30")])],"isStart":true}),makeQuery(id+"F5.opExtrude","CAP_FACE",FACE,{"disambiguationData":[OSD([sQuery(id+"F4.wireOp",EDGE,"E32")])],"isStart":true})]})],"blendedInto":[makeQuery(id+"F5.boolean.opBoolean","MERGE",FACE,{"derivedFrom":[makeQuery(id+"F1.opExtrude","SWEPT_FACE",FACE,{"disambiguationData":[OSD([sQuery(id+"F0.wireOp",EDGE,"E8")])]}),makeQuery(id+"F5.opExtrude","CAP_FACE",FACE,{"disambiguationData":[OSD([sQuery(id+"F4.wireOp",EDGE,"E30")])],"isStart":true}),makeQuery(id+"F5.opExtrude","CAP_FACE",FACE,{"disambiguationData":[OSD([sQuery(id+"F4.wireOp",EDGE,"E32")])],"isStart":true})]})]});
            var Q1;
            Q1=makeQuery(id+"F11.opFillet","BLEND_EDGE",EDGE,{"blendedFrom":[makeQuery(id+"F1.opExtrude","CAP_EDGE",EDGE,{"disambiguationData":[OSD([sQuery(id+"F0.wireOp",EDGE,"E16")])],"isStart":true}),makeQuery(id+"F1.opExtrude","SWEPT_FACE",FACE,{"disambiguationData":[OSD([sQuery(id+"F0.wireOp",EDGE,"E15.0")])]})],"blendedInto":[makeQuery(id+"F1.opExtrude","SWEPT_FACE",FACE,{"disambiguationData":[OSD([sQuery(id+"F0.wireOp",EDGE,"E15.0")])]})]});
            fillet(context, id + "F13", {"entities" : qUnion([Q0, Q1]), "radius" : 1 * mm, "tangentPropagation" : true, "allowEdgeOverflow" : false});
        }
    });
